# Revit family: Rohrschelle Titan HD, 1 Zoll, o.D
name_source: partatom
category: HLS-Bauteile
revit_build: Autodesk Revit 2017 (Build: 20190507_1515(x64)
units: mm (PartAtom-declared; Revit-internal decimal feet)

## family parameters
Arbeitsebenenbasiert = Nein
Beim Laden mit Abzugskörper schneiden = Nein
Bemaßung runder Anschluss = Durchmesser verwenden
Gemeinsam genutzt = Ja
Immer vertikal = Nein
Raumberechnungspunkt = Nein
Teiletyp = Normal

## types (21) — shared parameters
A = 25 mm  [stored 0.082021 ft]
Anschluss = 1''
Anschlußhöhe = 25 mm
Bauart = zweiteilig
Brandschutz = RAL GZ 656
DF1 = 29 mm  [stored 0.0951444 ft]
DVS = 13 mm
Fabrikat = MEFA
Firma = MEFA Befestigungs- und Montagesysteme GmbH
HGA = 20 mm  [stored 0.0656168 ft]
Kurztext1 = Rohrschelle Titan HD 50x5,0
MB = 50 mm  [stored 0.164042 ft]
MD = 5 mm  [stored 0.0164042 ft]
Material = Stahl
Materialmaße = 50x5,0 mm
Materialname = S235
Mengeneinheit = St
Oberflaeche = galvanisch verzinkt
Verschluss = Schraubverschluss
Verschluss-Schraube = M12
max. zul. Last horizontal = 0.00 kN
max. zul. Last vertikal = 0.00 kN
vpe = 1 St
zero-valued in all types: AB, Nennweite DN Rohr, Stärke Material, max. Rohraußendurchmesser, min. Rohraußendurchmesser

## per-type parameters (varying)
| type | Achsabstand | Artikelnummer | B | Breite | D | DF2 | EAN | Gewicht | Gewicht pro Bauteil | H | Höhe | Kurztext2 | R | RM | Rohraußendurchmesser | Rohraußendurchmesser Zoll | S | max. Höhe | max. zul. Last |
| Titan HD, 1", Ø 76, o.D. | 124 mm | 0074510 | 154 mm | 153 mm | 76 mm  [stored 0.249344 ft] | 13 mm | 4250928404350 | 0.90 kg | 0.90 kg | 106 mm  [stored 0.347769 ft] | 106 mm | 76 mm 1'' | 38 mm  [stored 0.124672 ft] | 43 mm | 76 mm  [stored 0.249344 ft] | 2 1/2 Zoll | 125 mm | 106 mm  [stored 0.347769 ft] | 6.00 kN |
| Titan HD, 1", Ø 64, o.D. | 112 mm | 0074505 | 141 mm | 141 mm | 64 mm  [stored 0.209974 ft] | 13 mm | 4250928404336 | 0.83 kg | 0.83 kg | 94 mm  [stored 0.308399 ft] | 94 mm | 64 mm 1'' | 32 mm  [stored 0.104987 ft] | 37 mm  [stored 0.121391 ft] | 64 mm  [stored 0.209974 ft] | Zoll | 112 mm | 94 mm  [stored 0.308399 ft] | 6.00 kN |
| Titan HD, 1", Ø 89, o.D. | 138 mm | 0074512 | 167 mm | 167 mm | 89 mm  [stored 0.291995 ft] | 13 mm | 4250928404374 | 0.99 kg | 0.99 kg | 119 mm | 119 mm | 89 mm 1'' | 45 mm | 50 mm  [stored 0.164042 ft] | 89 mm  [stored 0.291995 ft] | 3 Zoll | 138 mm | 119 mm | 6.00 kN |
| Titan HD, 1", Ø108, o.D. | 157 mm | 0074520 | 186 mm | 186 mm | 108 mm  [stored 0.354331 ft] | 13 mm | 4250928404404 | 1.11 kg | 1.11 kg | 138 mm | 138 mm | 108 mm 1'' | 54 mm  [stored 0.177165 ft] | 59 mm  [stored 0.19357 ft] | 108 mm  [stored 0.354331 ft] | Zoll | 157 mm | 138 mm | 6.00 kN |
| Titan HD, 1", Ø110, o.D. | 159 mm | 0074522 | 188 mm | 188 mm | 110 mm | 13 mm | 4250928404411 | 1.12 kg | 1.12 kg | 140 mm | 140 mm | 110 mm 1'' | 55 mm  [stored 0.180446 ft] | 60 mm  [stored 0.19685 ft] | 110 mm | Zoll | 159 mm | 140 mm | 6.00 kN |
| Titan HD, 1", Ø114, o.D. | 163 mm | 0074524 | 192 mm | 192 mm | 114 mm | 13 mm | 4250928404428 | 1.15 kg | 1.15 kg | 144 mm | 144 mm | 114 mm 1'' | 57 mm  [stored 0.187008 ft] | 62 mm  [stored 0.203412 ft] | 114 mm | 4 Zoll | 163 mm | 144 mm | 6.00 kN |
| Titan HD, 1", Ø133, o.D. | 183 mm | 0074587 | 212 mm | 212 mm | 133 mm | 14 mm  [stored 0.0459318 ft] | 4250928404466 | 1.27 kg | 1.27 kg | 163 mm | 163 mm | 133 mm 1'' | 67 mm | 72 mm | 133 mm | Zoll | 183 mm | 163 mm | 6.00 kN |
| Titan HD, 1", Ø135, o.D. | 185 mm | 0074595 | 214 mm | 214 mm | 135 mm | 14 mm  [stored 0.0459318 ft] | 4250928404480 | 1.28 kg | 1.28 kg | 165 mm | 165 mm | 135 mm 1'' | 68 mm | 73 mm | 135 mm | Zoll | 185 mm | 165 mm | 6.00 kN |
| Titan HD, 1", Ø140, o.D. | 190 mm | 0074609 | 219 mm | 219 mm | 140 mm | 14 mm  [stored 0.0459318 ft] | 4250928404503 | 1.31 kg | 1.31 kg | 170 mm | 170 mm | 140 mm 1'' | 70 mm  [stored 0.229659 ft] | 75 mm  [stored 0.246063 ft] | 140 mm | 5 Zoll | 190 mm | 170 mm | 6.00 kN |
| Titan HD, 1", Ø160, o.D. | 210 mm | 0074641 | 239 mm | 239 mm | 160 mm | 14 mm  [stored 0.0459318 ft] | 4250928404541 | 1.44 kg | 1.44 kg | 190 mm | 190 mm | 160 mm 1'' | 80 mm  [stored 0.262467 ft] | 85 mm  [stored 0.278871 ft] | 160 mm | Zoll | 210 mm | 190 mm | 6.00 kN |
| Titan HD, 1", Ø165, o.D. | 215 mm | 0074684 | 244 mm | 244 mm | 165 mm | 14 mm  [stored 0.0459318 ft] | 4250928404565 | 1.47 kg | 1.47 kg | 195 mm | 195 mm | 165 mm 1'' | 83 mm | 88 mm | 165 mm | 6 Zoll | 215 mm | 195 mm | 6.00 kN |
| Titan HD, 1", Ø168, o.D. | 218 mm | 0074686 | 247 mm | 247 mm | 168 mm | 14 mm  [stored 0.0459318 ft] | 4250928404572 | 1.49 kg | 1.49 kg | 198 mm | 198 mm | 168 mm 1'' | 84 mm  [stored 0.275591 ft] | 89 mm  [stored 0.291995 ft] | 168 mm | Zoll | 218 mm | 198 mm | 6.00 kN |
| Titan HD, 1", Ø194, o.D. | 244 mm | 0074757 | 273 mm | 273 mm | 194 mm | 14 mm  [stored 0.0459318 ft] | 4250928404626 | 1.65 kg | 1.65 kg | 224 mm | 224 mm | 194 mm 1'' | 97 mm  [stored 0.318241 ft] | 102 mm  [stored 0.334646 ft] | 194 mm | Zoll | 244 mm | 224 mm | 16.00 kN |
| Titan HD, 1", Ø200, o.D. | 250 mm | 0074773 | 279 mm | 279 mm | 200 mm | 14 mm  [stored 0.0459318 ft] | 4250928404640 | 1.69 kg | 1.69 kg | 230 mm | 230 mm | 200 mm 1'' | 100 mm  [stored 0.328084 ft] | 105 mm  [stored 0.344488 ft] | 200 mm | Zoll | 250 mm | 230 mm | 16.00 kN |
| Titan HD, 1", Ø210, o.D. | 261 mm | 0074781 | 290 mm | 290 mm | 210 mm | 14 mm  [stored 0.0459318 ft] | 4250928404664 | 1.76 kg | 1.76 kg | 240 mm | 240 mm | 210 mm 1'' | 105 mm  [stored 0.344488 ft] | 110 mm | 210 mm | Zoll | 261 mm | 240 mm | 16.00 kN |
| Titan HD, 1", Ø219, o.D. | 270 mm | 0074803 | 299 mm | 299 mm | 219 mm | 14 mm  [stored 0.0459318 ft] | 4250928404688 | 1.81 kg | 1.81 kg | 249 mm | 249 mm | 219 mm 1'' | 110 mm | 115 mm | 219 mm | 8 Zoll | 270 mm | 249 mm | 16.00 kN |
| Titan HD, 1", Ø267, o.D. | 318 mm | 0074874 | 347 mm | 347 mm | 267 mm | 14 mm  [stored 0.0459318 ft] | 4250928404725 | 2.12 kg | 2.12 kg | 297 mm | 297 mm | 267 mm 1'' | 134 mm | 139 mm | 267 mm | Zoll | 318 mm | 297 mm | 16.00 kN |
| Titan HD, 1", Ø273, o.D. | 324 mm | 0074897 | 353 mm | 353 mm | 273 mm | 14 mm  [stored 0.0459318 ft] | 4250928404749 | 2.16 kg | 2.16 kg | 303 mm | 303 mm | 273 mm 1'' | 137 mm | 142 mm | 273 mm | 10 Zoll | 324 mm | 303 mm | 16.00 kN |
| Titan HD, 1", Ø324, o.D. | 375 mm | 0074939 | 404 mm | 404 mm | 324 mm | 14 mm  [stored 0.0459318 ft] | 4250928404787 | 2.48 kg | 2.48 kg | 354 mm | 354 mm | 324 mm 1'' | 162 mm | 167 mm | 324 mm | 12 Zoll | 375 mm | 354 mm | 16.00 kN |
| Titan HD, 1", Ø356, o.D. | 407 mm | 0074968 | 436 mm | 436 mm | 356 mm | 14 mm  [stored 0.0459318 ft] | 4250928404800 | 2.68 kg | 2.68 kg | 386 mm | 386 mm | 356 mm 1'' | 178 mm | 183 mm | 356 mm | Zoll | 407 mm | 386 mm | 16.00 kN |
| Titan HD, 1", Ø368, o.D. | 419 mm | 0074970 | 448 mm | 448 mm | 368 mm | 14 mm  [stored 0.0459318 ft] | 4250928404824 | 2.76 kg | 2.76 kg | 398 mm | 398 mm | 368 mm 1'' | 184 mm | 189 mm | 368 mm | 14 Zoll | 419 mm | 398 mm | 16.00 kN |

note: [stored X ft] marks values corroborated as IEEE doubles in the binary element streams (Revit-internal decimal feet)

## geometry (parser evidence)
native form markers: Sweep x6
no freeform markers — native parametric forms only
